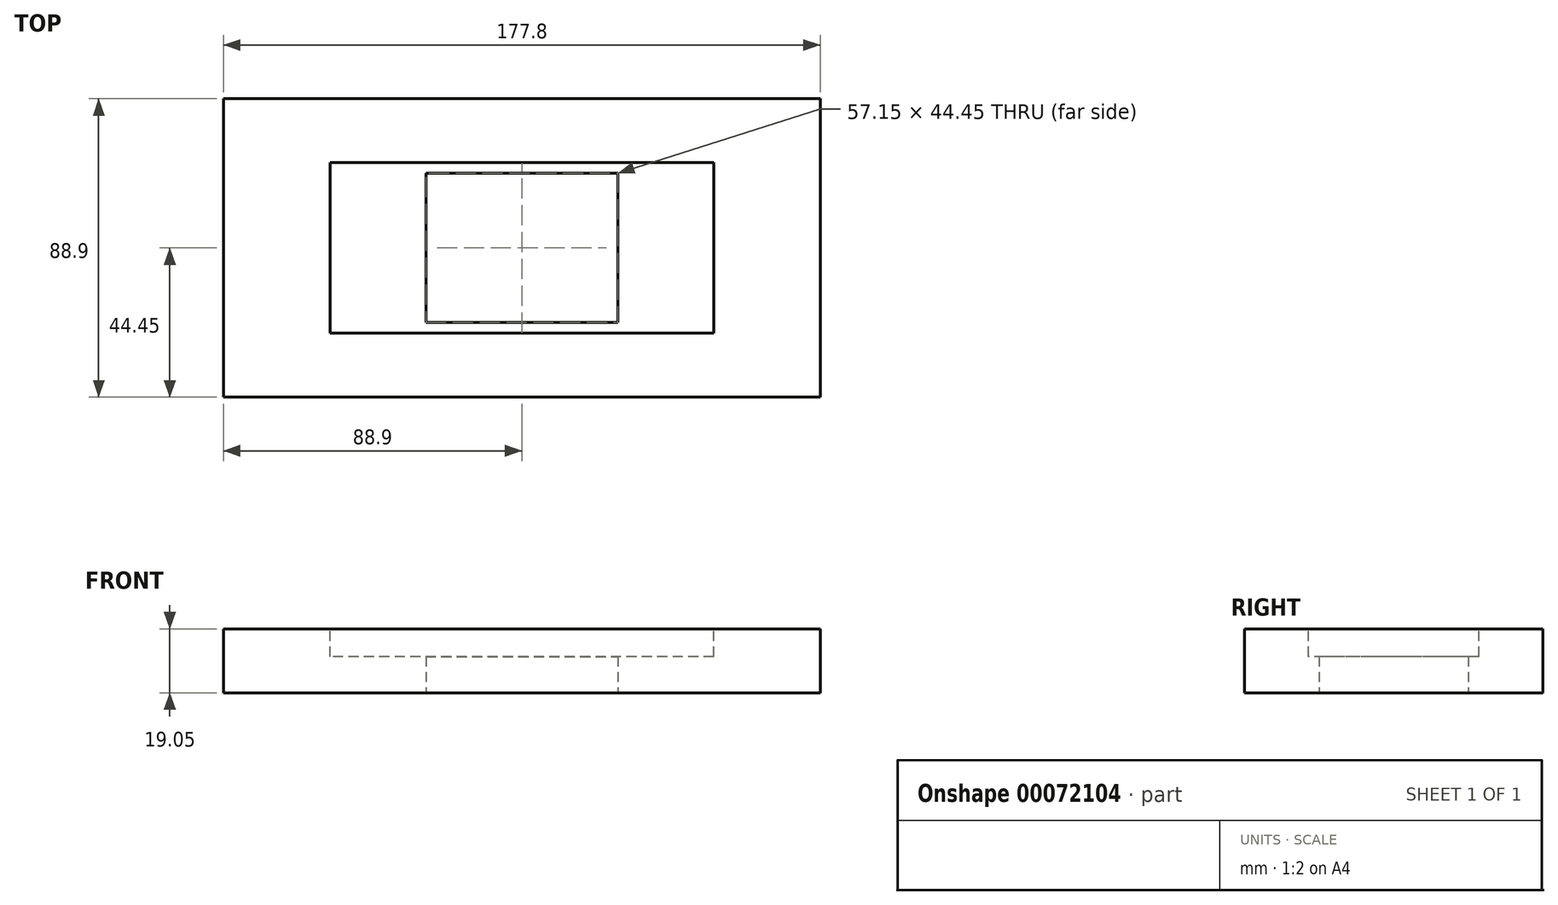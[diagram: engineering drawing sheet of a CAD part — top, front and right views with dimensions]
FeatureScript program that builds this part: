
annotation { "Feature Type Name" : "Feature", "Feature Type Description" : "" }
export const myFeature = defineFeature(function(context is Context, id is Id, definition is map)
    precondition{}
    {
        {
            var Q0;
            Q0=qCreatedBy(makeId("Top.planeOp"),FACE);
            var sketch = newSketch(context, id + "F0", { "sketchPlane" : qUnion([Q0])});
            skLineSegment(sketch, "E0.rect.bottom", {"start": v(88.9, 44.45) * mm, "end": v(-88.9, 44.45) * mm});
            skLineSegment(sketch, "E0.rect.top", {"start": v(88.9, -44.45) * mm, "end": v(-88.9, -44.45) * mm});
            skLineSegment(sketch, "E0.rect.left", {"start": v(88.9, 44.45) * mm, "end": v(88.9, -44.45) * mm});
            skLineSegment(sketch, "E0.rect.right", {"start": v(-88.9, 44.45) * mm, "end": v(-88.9, -44.45) * mm});
            skPoint(sketch, "E0.rect.middle", {"position": v(0, 0) * mm});
            skSolve(sketch);
        }
        {
            var Q0;
            Q0 = qSketchRegion(id + "F0", true);
            extrude(context, id + "F1", {"entities" : qUnion([Q0]), "depth" : 19.05 * mm});
        }
        {
            var Q0;
            Q0=makeQuery(id+"F1.opExtrude","CAP_FACE",FACE,{"disambiguationData":[OSD([sQuery(id+"F0.wireOp",EDGE,"E0.rect.bottom"),sQuery(id+"F0.wireOp",EDGE,"E0.rect.top"),sQuery(id+"F0.wireOp",EDGE,"E0.rect.left"),sQuery(id+"F0.wireOp",EDGE,"E0.rect.right")])],"isStart":false});
            var sketch = newSketch(context, id + "F2", { "sketchPlane" : qUnion([Q0])});
            skLineSegment(sketch, "E1.rect.bottom", {"start": v(57.15, 25.4) * mm, "end": v(-57.15, 25.4) * mm});
            skLineSegment(sketch, "E1.rect.top", {"start": v(57.15, -25.4) * mm, "end": v(-57.15, -25.4) * mm});
            skLineSegment(sketch, "E1.rect.left", {"start": v(57.15, 25.4) * mm, "end": v(57.15, -25.4) * mm});
            skLineSegment(sketch, "E1.rect.right", {"start": v(-57.15, 25.4) * mm, "end": v(-57.15, -25.4) * mm});
            skPoint(sketch, "E1.rect.middle", {"position": v(0, 0) * mm});
            skSolve(sketch);
        }
        {
            var Q0;
            Q0 = qSketchRegion(id + "F2", true);
            extrude(context, id + "F3", {"entities" : qUnion([Q0]), "operationType" : NewBodyOperationType.REMOVE, "oppositeDirection" : true, "depth" : 8.25 * mm});
        }
        {
            var Q0;
            Q0=makeQuery(id+"F1.opExtrude","CAP_FACE",FACE,{"disambiguationData":[OSD([sQuery(id+"F0.wireOp",EDGE,"E0.rect.bottom"),sQuery(id+"F0.wireOp",EDGE,"E0.rect.top"),sQuery(id+"F0.wireOp",EDGE,"E0.rect.left"),sQuery(id+"F0.wireOp",EDGE,"E0.rect.right")])],"isStart":true});
            var sketch = newSketch(context, id + "F4", { "sketchPlane" : qUnion([Q0])});
            skLineSegment(sketch, "E2.rect.bottom", {"start": v(28.58, 22.23) * mm, "end": v(-28.58, 22.23) * mm});
            skLineSegment(sketch, "E2.rect.top", {"start": v(28.58, -22.23) * mm, "end": v(-28.58, -22.23) * mm});
            skLineSegment(sketch, "E2.rect.left", {"start": v(28.58, 22.23) * mm, "end": v(28.58, -22.23) * mm});
            skLineSegment(sketch, "E2.rect.right", {"start": v(-28.58, 22.23) * mm, "end": v(-28.58, -22.23) * mm});
            skPoint(sketch, "E2.rect.middle", {"position": v(0, 0) * mm});
            skSolve(sketch);
        }
        {
            var Q0;
            Q0 = qSketchRegion(id + "F4", true);
            extrude(context, id + "F5", {"entities" : qUnion([Q0]), "operationType" : NewBodyOperationType.REMOVE, "endBound" : BoundingType.THROUGH_ALL, "oppositeDirection" : true, "depth" : 25.4 * mm});
        }
    });
